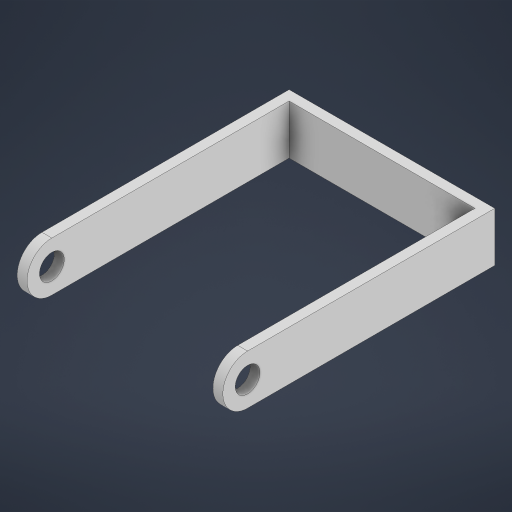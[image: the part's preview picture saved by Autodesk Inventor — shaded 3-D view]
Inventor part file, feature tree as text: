
AUTODESK INVENTOR PART (.ipt)
format: ipt  version: 2024 (Build 280153000, 153)  size: 199,168 bytes
history: native  units: mm
features: extrude x3, sketch x3, other x1
ambient origin geometry x8: Origin, YZ Plane, XZ Plane, XY Plane, X Axis, Y Axis, Z Axis, Center Point
bodies: Body1 (feature_tree)
feature tree (7):
  other  "솔리드1"
  extrude  "돌출1"  Depth=5.0mm
  extrude  "돌출2"  Depth=10.0mm
  extrude  "돌출3"  Depth=10.0mm
  sketch  "스케치1"
  sketch  "스케치2"
  sketch  "스케치3"
